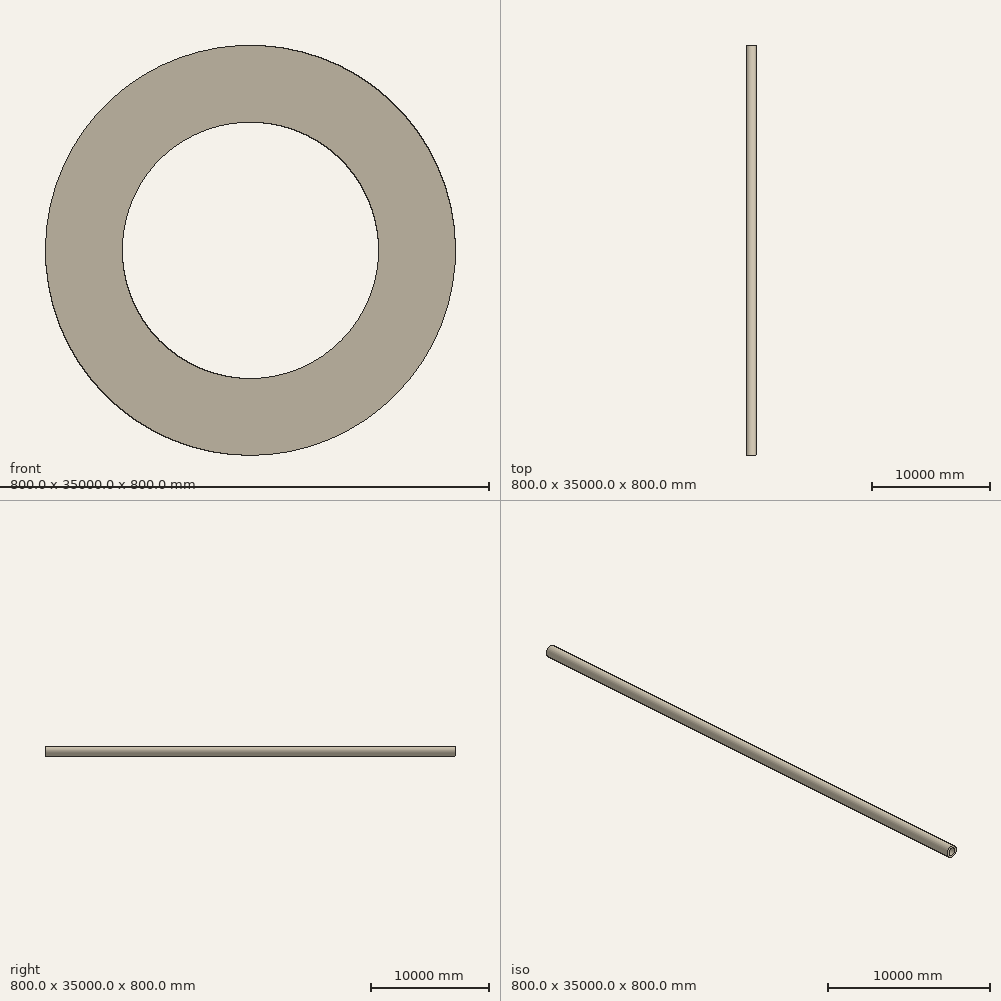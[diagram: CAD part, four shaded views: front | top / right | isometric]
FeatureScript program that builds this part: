
annotation { "Feature Type Name" : "Feature", "Feature Type Description" : "" }
export const myFeature = defineFeature(function(context is Context, id is Id, definition is map)
    precondition{}
    {
        {
            var Q0;
            Q0=qCreatedBy(makeId("Front.planeOp"),FACE);
            var sketch = newSketch(context, id + "F0", { "sketchPlane" : qUnion([Q0])});
            skCircle(sketch, "E0", {"center": v(0, 0) * mm, "radius": 250 * mm});
            skCircle(sketch, "E1.0", {"center": v(0, 0) * mm, "radius": 400 * mm});
            skSolve(sketch);
        }
        {
            var Q0;
            Q0=makeQuery(id+"F0.imprint","IMPRINT",FACE,{"disambiguationData":[TD([[makeQuery(id+"F0.imprint","IMPRINT",EDGE,{"derivedFrom":sQuery(id+"F0.wireOp",EDGE,"E0")}),-1.0]])]});
            extrude(context, id + "F1", {"entities" : qUnion([Q0]), "depth" : 35000 * mm});
        }
    });
